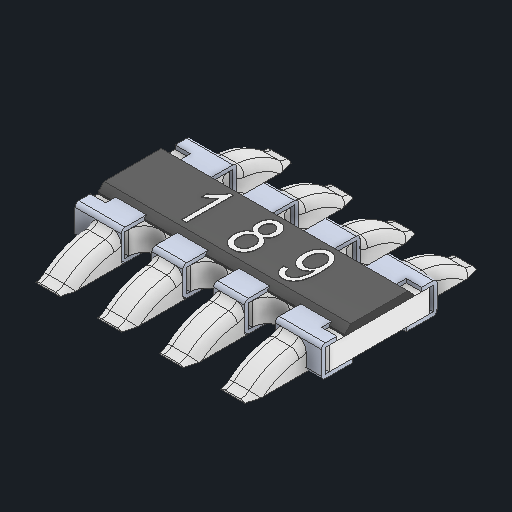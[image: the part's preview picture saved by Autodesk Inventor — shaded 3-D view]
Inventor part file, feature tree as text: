
AUTODESK INVENTOR PART (.ipt)
format: ipt  version: 2023 (Build 270158000, 158)  size: 557,568 bytes
history: native  units: in
note: dims shown in document units (in); Inventor stores cm internally (conversion verified against a paired STEP export)
features: other x8, fillet x2
ambient origin geometry x8: Origin, YZ Plane, XZ Plane, XY Plane, X Axis, Y Axis, Z Axis, Center Point
bodies: Solid1 (feature_tree), Solid2 (feature_tree), Solid3 (feature_tree), Solid4 (feature_tree), Solid5 (feature_tree), Solid6 (feature_tree), Solid7 (feature_tree), Solid8 (feature_tree), Solid9 (feature_tree), Solid10 (feature_tree)
feature tree (10):
  other  "Cut-Extrude7"
  other  "Boss-Extrude5"
  fillet  "Fillet2"  [1 undecoded]
  fillet  "Fillet1"  [1 undecoded]
  other  "LPattern3[1]"
  other  "LPattern3[2]"
  other  "LPattern3[3]"
  other  "LPattern3[4]"
  other  "LPattern3[5]"
  other  "LPattern3[6]"
note: 2 required parameter values undecoded (feature->parameter linkage not recoverable at this tier; creation-order binding heuristic only, values carry confidence <= 0.55)
